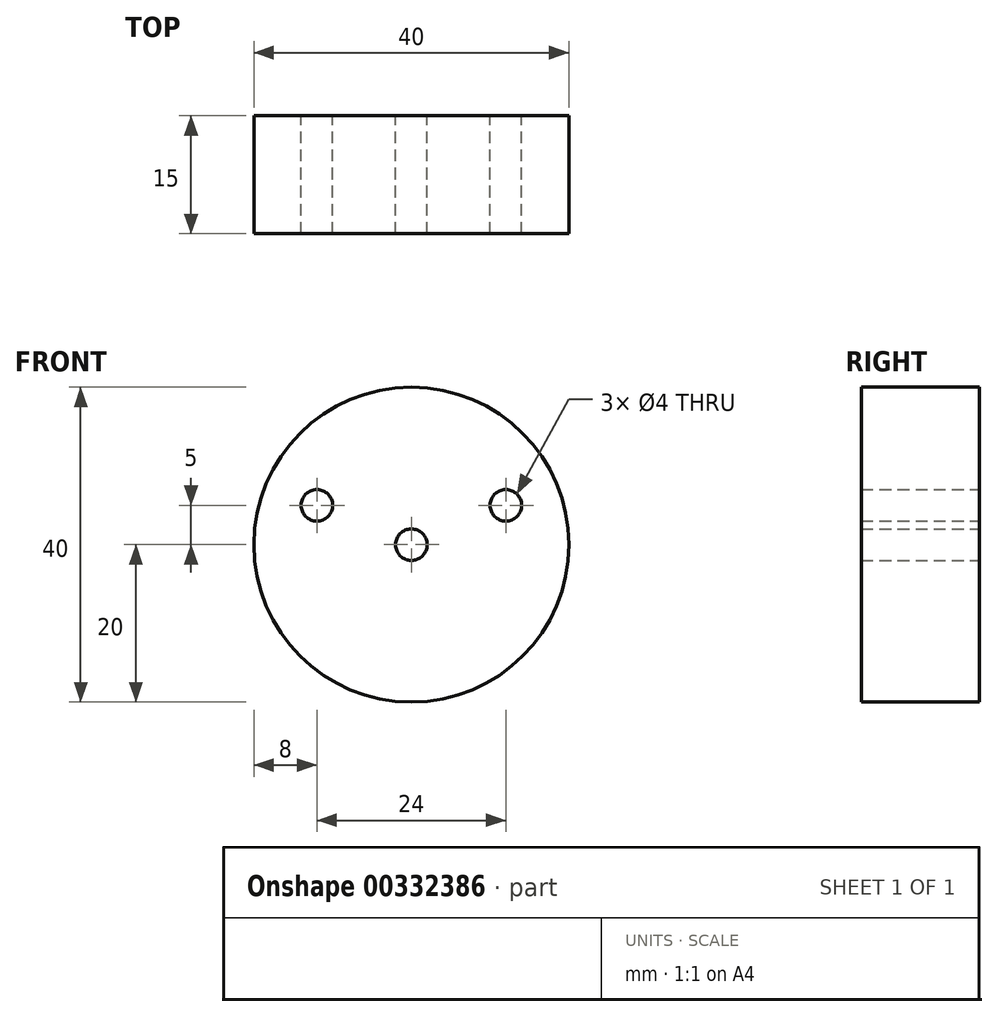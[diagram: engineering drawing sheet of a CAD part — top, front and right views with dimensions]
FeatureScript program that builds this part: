
annotation { "Feature Type Name" : "Feature", "Feature Type Description" : "" }
export const myFeature = defineFeature(function(context is Context, id is Id, definition is map)
    precondition{}
    {
        {
            var Q0;
            Q0=qCreatedBy(makeId("Front.planeOp"),FACE);
            var sketch = newSketch(context, id + "F0", { "sketchPlane" : qUnion([Q0])});
            skCircle(sketch, "E0", {"center": v(0, 0) * mm, "radius": 20 * mm});
            skCircle(sketch, "E1", {"center": v(0, 0) * mm, "radius": 2 * mm});
            skCircle(sketch, "E2", {"center": v(-12, 5) * mm, "radius": 2 * mm});
            skCircle(sketch, "E3", {"center": v(12, 5) * mm, "radius": 2 * mm});
            skSolve(sketch);
        }
        {
            var Q0;
            Q0=makeQuery(id+"F0.imprint","IMPRINT",FACE,{"disambiguationData":[TD([[makeQuery(id+"F0.imprint","IMPRINT",EDGE,{"derivedFrom":sQuery(id+"F0.wireOp",EDGE,"E0")}),1.0]])]});
            extrude(context, id + "F1", {"entities" : qUnion([Q0]), "depth" : 15 * mm});
        }
    });
